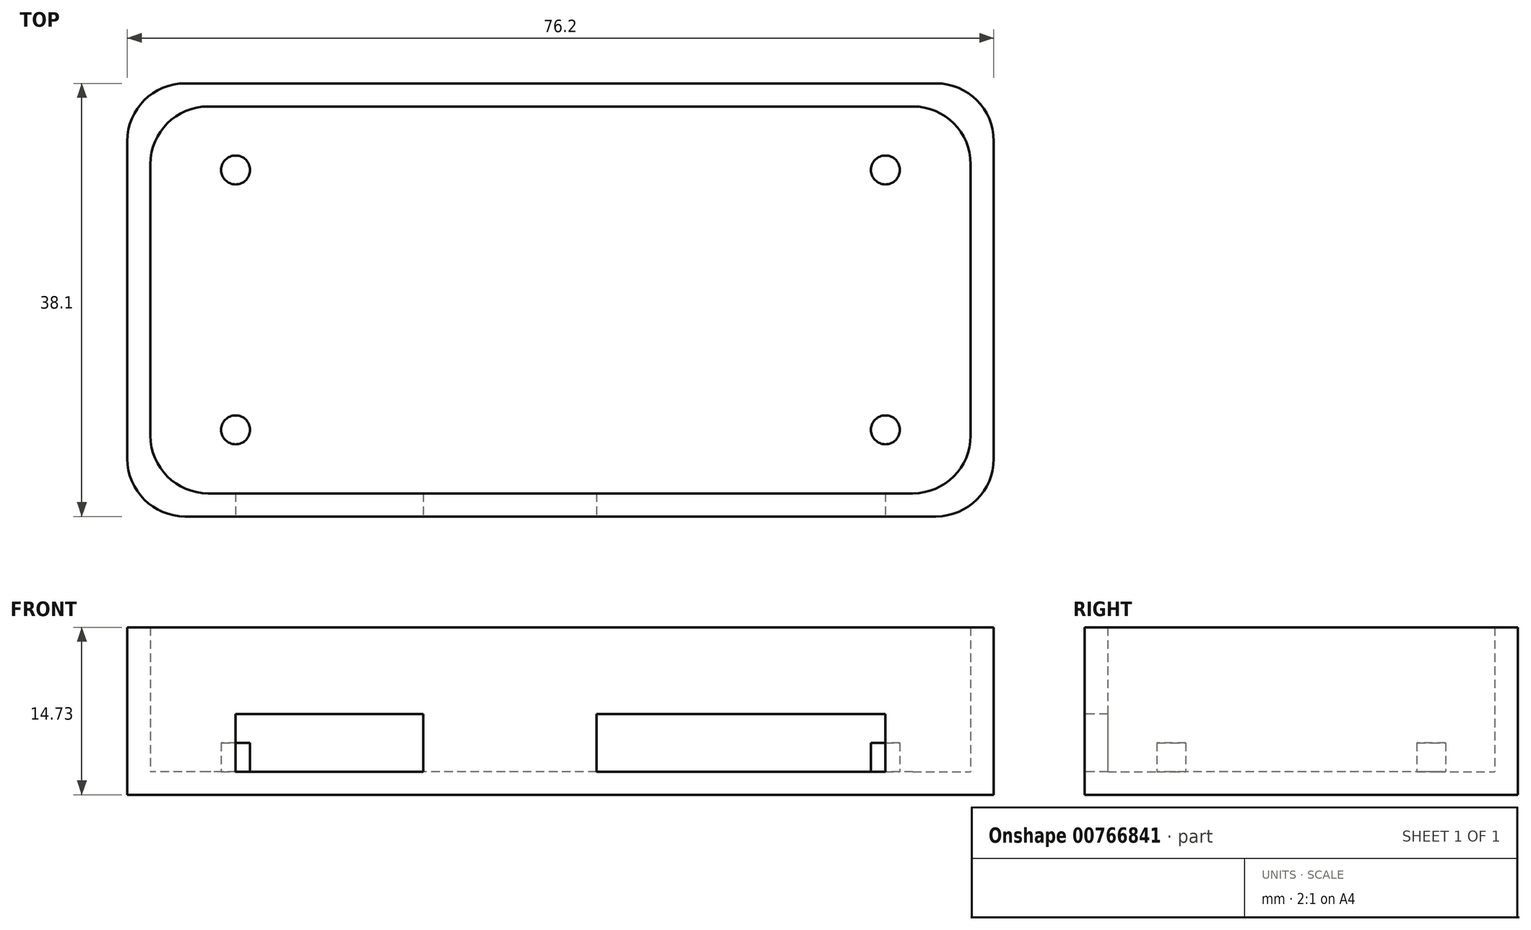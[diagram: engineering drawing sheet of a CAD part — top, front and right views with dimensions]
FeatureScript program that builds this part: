
annotation { "Feature Type Name" : "Feature", "Feature Type Description" : "" }
export const myFeature = defineFeature(function(context is Context, id is Id, definition is map)
    precondition{}
    {
        {
            var Q0;
            Q0=qCreatedBy(makeId("Top.planeOp"),FACE);
            var sketch = newSketch(context, id + "F0", { "sketchPlane" : qUnion([Q0])});
            skLineSegment(sketch, "E0.bottom", {"start": v(38.1, 19.05) * mm, "end": v(-38.1, 19.05) * mm});
            skLineSegment(sketch, "E0.top", {"start": v(38.1, -19.05) * mm, "end": v(-38.1, -19.05) * mm});
            skLineSegment(sketch, "E0.left", {"start": v(38.1, 19.05) * mm, "end": v(38.1, -19.05) * mm});
            skLineSegment(sketch, "E0.right", {"start": v(-38.1, 19.05) * mm, "end": v(-38.1, -19.05) * mm});
            skPoint(sketch, "E0.middle", {"position": v(0, 0) * mm});
            skSolve(sketch);
        }
        {
            var Q0;
            Q0=makeQuery(id+"F0.imprint","IMPRINT",FACE,{"disambiguationData":[TD([[makeQuery(id+"F0.imprint","IMPRINT",EDGE,{"derivedFrom":sQuery(id+"F0.wireOp",EDGE,"E0.bottom")}),1.0]])]});
            extrude(context, id + "F1", {"entities" : qUnion([Q0]), "depth" : 2.03 * mm, "offsetDistance" : 25.4 * mm});
        }
        {
            var Q0;
            Q0=makeQuery(id+"F1.opExtrude","CAP_FACE",FACE,{"disambiguationData":[OSD([sQuery(id+"F0.wireOp",EDGE,"E0.bottom"),sQuery(id+"F0.wireOp",EDGE,"E0.top"),sQuery(id+"F0.wireOp",EDGE,"E0.left"),sQuery(id+"F0.wireOp",EDGE,"E0.right")])],"isStart":false});
            var sketch = newSketch(context, id + "F2", { "sketchPlane" : qUnion([Q0])});
            skLineSegment(sketch, "E1.bottom", {"start": v(36.07, 17.02) * mm, "end": v(-36.07, 17.02) * mm});
            skLineSegment(sketch, "E1.top", {"start": v(36.07, -17.02) * mm, "end": v(-36.07, -17.02) * mm});
            skLineSegment(sketch, "E1.left", {"start": v(36.07, 17.02) * mm, "end": v(36.07, -17.02) * mm});
            skLineSegment(sketch, "E1.right", {"start": v(-36.07, 17.02) * mm, "end": v(-36.07, -17.02) * mm});
            skPoint(sketch, "E1.middle", {"position": v(0, 0) * mm});
            skSolve(sketch);
        }
        {
            var Q0;
            Q0=makeQuery(id+"F2.imprint","IMPRINT",FACE,{"disambiguationData":[TD([[makeQuery(id+"F2.imprint","IMPRINT",EDGE,{"derivedFrom":sQuery(id+"F2.wireOp",EDGE,"E1.bottom")}),-1.0]])]});
            extrude(context, id + "F3", {"entities" : qUnion([Q0]), "operationType" : NewBodyOperationType.ADD, "depth" : 12.7 * mm, "offsetDistance" : 25.4 * mm});
        }
        {
            var Q0;
            Q0=makeQuery(id+"F1.opExtrude","CAP_FACE",FACE,{"disambiguationData":[OSD([sQuery(id+"F0.wireOp",EDGE,"E0.bottom"),sQuery(id+"F0.wireOp",EDGE,"E0.top"),sQuery(id+"F0.wireOp",EDGE,"E0.left"),sQuery(id+"F0.wireOp",EDGE,"E0.right")])],"isStart":false});
            var sketch = newSketch(context, id + "F4", { "sketchPlane" : qUnion([Q0])});
            skLineSegment(sketch, "E2.bottom", {"start": v(28.57, 11.43) * mm, "end": v(-28.57, 11.43) * mm, "construction": true});
            skLineSegment(sketch, "E2.top", {"start": v(28.57, -11.43) * mm, "end": v(-28.57, -11.43) * mm, "construction": true});
            skLineSegment(sketch, "E2.left", {"start": v(28.57, 11.43) * mm, "end": v(28.57, -11.43) * mm, "construction": true});
            skLineSegment(sketch, "E2.right", {"start": v(-28.57, 11.43) * mm, "end": v(-28.57, -11.43) * mm, "construction": true});
            skPoint(sketch, "E2.middle", {"position": v(0, 0) * mm});
            skCircle(sketch, "E3", {"center": v(-28.57, 11.43) * mm, "radius": 1.27 * mm});
            skCircle(sketch, "E4", {"center": v(28.57, 11.43) * mm, "radius": 1.27 * mm});
            skCircle(sketch, "E5", {"center": v(28.57, -11.43) * mm, "radius": 1.27 * mm});
            skCircle(sketch, "E6", {"center": v(-28.57, -11.43) * mm, "radius": 1.27 * mm});
            skSolve(sketch);
        }
        {
            var Q0;
            Q0=makeQuery(id+"F4.imprint","IMPRINT",FACE,{"disambiguationData":[TD([[makeQuery(id+"F4.imprint","IMPRINT",EDGE,{"derivedFrom":sQuery(id+"F4.wireOp",EDGE,"E3")}),1.0]])]});
            var Q1;
            Q1=makeQuery(id+"F4.imprint","IMPRINT",FACE,{"disambiguationData":[TD([[makeQuery(id+"F4.imprint","IMPRINT",EDGE,{"derivedFrom":sQuery(id+"F4.wireOp",EDGE,"E6")}),1.0]])]});
            var Q2;
            Q2=makeQuery(id+"F4.imprint","IMPRINT",FACE,{"disambiguationData":[TD([[makeQuery(id+"F4.imprint","IMPRINT",EDGE,{"derivedFrom":sQuery(id+"F4.wireOp",EDGE,"E5")}),1.0]])]});
            var Q3;
            Q3=makeQuery(id+"F4.imprint","IMPRINT",FACE,{"disambiguationData":[TD([[makeQuery(id+"F4.imprint","IMPRINT",EDGE,{"derivedFrom":sQuery(id+"F4.wireOp",EDGE,"E4")}),1.0]])]});
            extrude(context, id + "F5", {"entities" : qUnion([Q0, Q1, Q2, Q3]), "operationType" : NewBodyOperationType.ADD, "depth" : 2.54 * mm, "offsetDistance" : 25.4 * mm});
        }
        {
            var Q0;
            {var subQ0=sQuery(id+"F0.wireOp",EDGE,"E0.top");Q0=makeQuery(id+"F3.boolean.opBoolean","MERGE",FACE,{"derivedFrom":[makeQuery(id+"F1.opExtrude","SWEPT_FACE",FACE,{"disambiguationData":[OSD([subQ0])]}),makeQuery(id+"F3.opExtrude","SWEPT_FACE",FACE,{"disambiguationData":[OSD([subQ0])]})]});}
            var sketch = newSketch(context, id + "F6", { "sketchPlane" : qUnion([Q0])});
            skLineSegment(sketch, "E7", {"start": v(-38.1, 2.03) * mm, "end": v(38.1, 2.03) * mm, "construction": true});
            skLineSegment(sketch, "E8", {"start": v(-38.1, 7.11) * mm, "end": v(38.1, 7.11) * mm, "construction": true});
            skLineSegment(sketch, "E9", {"start": v(-28.58, 0) * mm, "end": v(-28.58, 14.73) * mm, "construction": true});
            skLineSegment(sketch, "E10", {"start": v(28.58, 0) * mm, "end": v(28.58, 14.73) * mm, "construction": true});
            skLineSegment(sketch, "E11", {"start": v(-12.07, 14.73) * mm, "end": v(-12.06, 0) * mm, "construction": true});
            skLineSegment(sketch, "E12", {"start": v(3.17, 14.73) * mm, "end": v(3.18, 0) * mm, "construction": true});
            skLineSegment(sketch, "E13.bottom", {"start": v(-28.58, 7.11) * mm, "end": v(-12.06, 7.11) * mm});
            skLineSegment(sketch, "E13.top", {"start": v(-28.58, 2.03) * mm, "end": v(-12.06, 2.03) * mm});
            skLineSegment(sketch, "E13.left", {"start": v(-28.58, 7.11) * mm, "end": v(-28.58, 2.03) * mm});
            skLineSegment(sketch, "E13.right", {"start": v(-12.06, 7.11) * mm, "end": v(-12.06, 2.03) * mm});
            skLineSegment(sketch, "E14.bottom", {"start": v(3.18, 7.11) * mm, "end": v(28.58, 7.11) * mm});
            skLineSegment(sketch, "E14.top", {"start": v(3.18, 2.03) * mm, "end": v(28.58, 2.03) * mm});
            skLineSegment(sketch, "E14.left", {"start": v(3.18, 7.11) * mm, "end": v(3.18, 2.03) * mm});
            skLineSegment(sketch, "E14.right", {"start": v(28.58, 7.11) * mm, "end": v(28.58, 2.03) * mm});
            skSolve(sketch);
        }
        {
            var Q0;
            Q0=makeQuery(id+"F6.imprint","IMPRINT",FACE,{"disambiguationData":[TD([[makeQuery(id+"F6.imprint","IMPRINT",EDGE,{"derivedFrom":sQuery(id+"F6.wireOp",EDGE,"E13.bottom")}),-1.0]])]});
            var Q1;
            Q1=makeQuery(id+"F6.imprint","IMPRINT",FACE,{"disambiguationData":[TD([[makeQuery(id+"F6.imprint","IMPRINT",EDGE,{"derivedFrom":sQuery(id+"F6.wireOp",EDGE,"E14.bottom")}),-1.0]])]});
            extrude(context, id + "F7", {"entities" : qUnion([Q0, Q1]), "operationType" : NewBodyOperationType.REMOVE, "oppositeDirection" : true, "depth" : 2.03 * mm, "offsetDistance" : 25.4 * mm});
        }
        {
            var Q0;
            Q0=makeQuery(id+"F3.opExtrude","SWEPT_EDGE",EDGE,{"disambiguationData":[OSD([sQuery(id+"F2.wireOp",EDGE,"E1.bottom"),sQuery(id+"F2.wireOp",EDGE,"E1.right")])]});
            var Q1;
            Q1=makeQuery(id+"F3.opExtrude","SWEPT_EDGE",EDGE,{"disambiguationData":[OSD([sQuery(id+"F2.wireOp",EDGE,"E1.top"),sQuery(id+"F2.wireOp",EDGE,"E1.right")])]});
            var Q2;
            Q2=makeQuery(id+"F3.opExtrude","SWEPT_EDGE",EDGE,{"disambiguationData":[OSD([sQuery(id+"F2.wireOp",EDGE,"E1.bottom"),sQuery(id+"F2.wireOp",EDGE,"E1.left")])]});
            var Q3;
            Q3=makeQuery(id+"F3.opExtrude","SWEPT_EDGE",EDGE,{"disambiguationData":[OSD([sQuery(id+"F2.wireOp",EDGE,"E1.top"),sQuery(id+"F2.wireOp",EDGE,"E1.left")])]});
            fillet(context, id + "F8", {"entities" : qUnion([Q0, Q1, Q2, Q3]), "radius" : 5.08 * mm, "tangentPropagation" : true, "allowEdgeOverflow" : false});
        }
        {
            var Q0;
            {var subQ0=sQuery(id+"F0.wireOp",EDGE,"E0.right");var subQ1=sQuery(id+"F0.wireOp",EDGE,"E0.top");Q0=makeQuery(id+"F3.boolean.opBoolean","MERGE",EDGE,{"derivedFrom":[makeQuery(id+"F1.opExtrude","SWEPT_EDGE",EDGE,{"disambiguationData":[OSD([subQ1,subQ0])]}),makeQuery(id+"F3.opExtrude","SWEPT_EDGE",EDGE,{"disambiguationData":[OSD([subQ1,subQ0])]})]});}
            var Q1;
            {var subQ0=sQuery(id+"F0.wireOp",EDGE,"E0.left");var subQ1=sQuery(id+"F0.wireOp",EDGE,"E0.top");Q1=makeQuery(id+"F3.boolean.opBoolean","MERGE",EDGE,{"derivedFrom":[makeQuery(id+"F1.opExtrude","SWEPT_EDGE",EDGE,{"disambiguationData":[OSD([subQ1,subQ0])]}),makeQuery(id+"F3.opExtrude","SWEPT_EDGE",EDGE,{"disambiguationData":[OSD([subQ1,subQ0])]})]});}
            var Q2;
            {var subQ0=sQuery(id+"F0.wireOp",EDGE,"E0.left");var subQ1=sQuery(id+"F0.wireOp",EDGE,"E0.bottom");Q2=makeQuery(id+"F3.boolean.opBoolean","MERGE",EDGE,{"derivedFrom":[makeQuery(id+"F1.opExtrude","SWEPT_EDGE",EDGE,{"disambiguationData":[OSD([subQ1,subQ0])]}),makeQuery(id+"F3.opExtrude","SWEPT_EDGE",EDGE,{"disambiguationData":[OSD([subQ1,subQ0])]})]});}
            var Q3;
            {var subQ0=sQuery(id+"F0.wireOp",EDGE,"E0.right");var subQ1=sQuery(id+"F0.wireOp",EDGE,"E0.bottom");Q3=makeQuery(id+"F3.boolean.opBoolean","MERGE",EDGE,{"derivedFrom":[makeQuery(id+"F1.opExtrude","SWEPT_EDGE",EDGE,{"disambiguationData":[OSD([subQ1,subQ0])]}),makeQuery(id+"F3.opExtrude","SWEPT_EDGE",EDGE,{"disambiguationData":[OSD([subQ1,subQ0])]})]});}
            fillet(context, id + "F9", {"entities" : qUnion([Q0, Q1, Q2, Q3]), "radius" : 5.08 * mm, "tangentPropagation" : true, "allowEdgeOverflow" : false});
        }
    });
